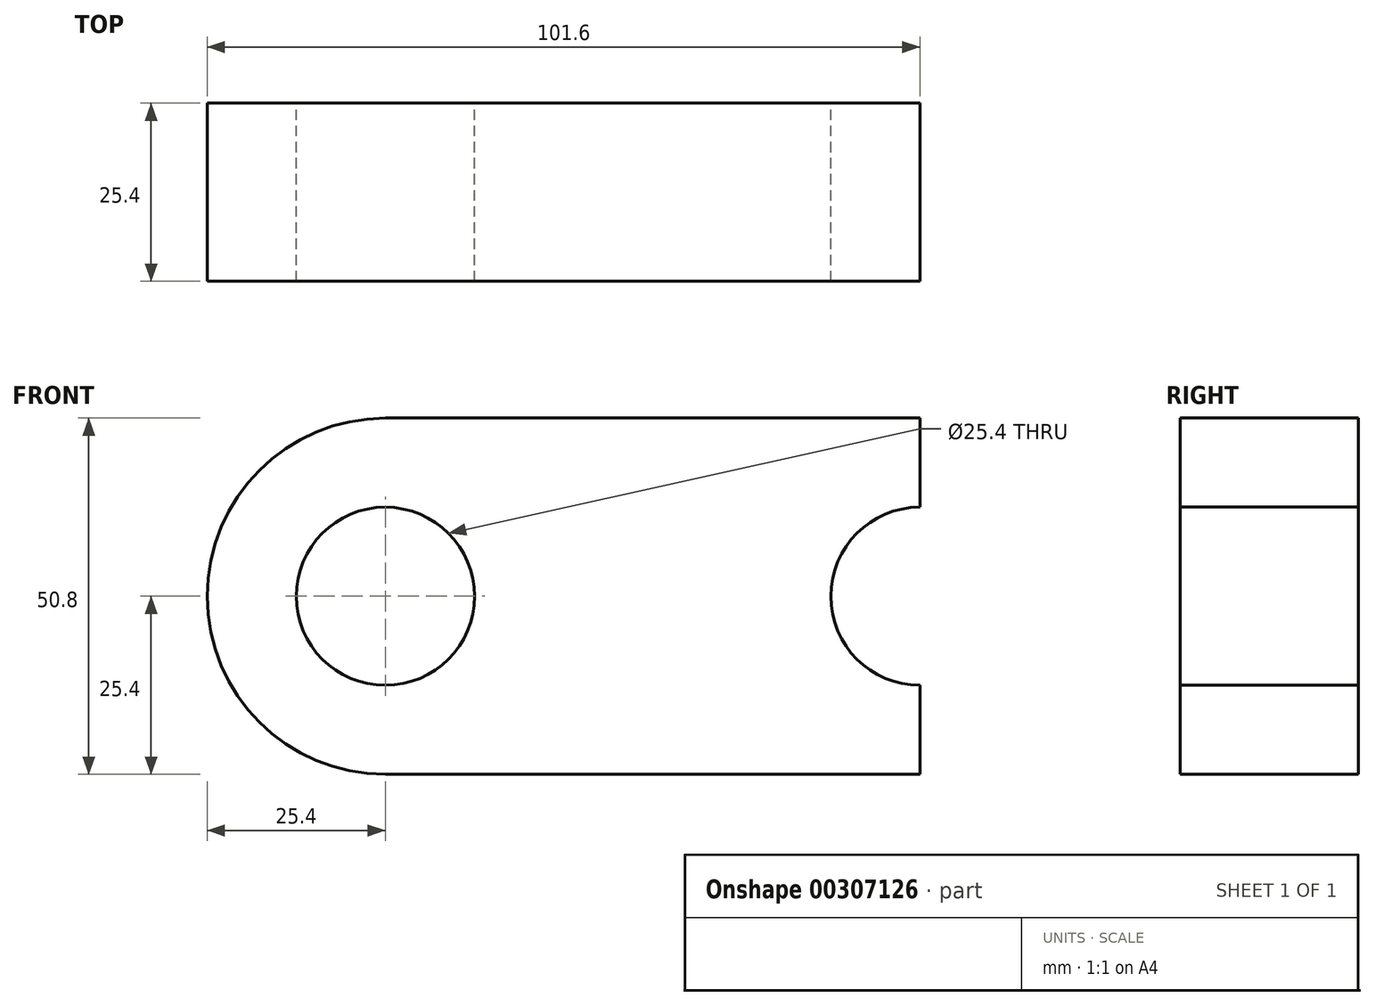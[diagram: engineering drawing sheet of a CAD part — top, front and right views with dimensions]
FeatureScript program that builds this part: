
annotation { "Feature Type Name" : "Feature", "Feature Type Description" : "" }
export const myFeature = defineFeature(function(context is Context, id is Id, definition is map)
    precondition{}
    {
        {
            var Q0;
            Q0=qCreatedBy(makeId("Front.planeOp"),FACE);
            var sketch = newSketch(context, id + "F0", { "sketchPlane" : qUnion([Q0])});
            skLineSegment(sketch, "E0.bottom", {"start": v(-38.1, 25.4) * mm, "end": v(38.1, 25.4) * mm});
            skLineSegment(sketch, "E0.top", {"start": v(-38.1, -25.4) * mm, "end": v(38.1, -25.4) * mm});
            skLineSegment(sketch, "E0.left", {"start": v(-38.1, 25.4) * mm, "end": v(-38.1, -25.4) * mm});
            skLineSegment(sketch, "E0.right", {"start": v(38.1, 25.4) * mm, "end": v(38.1, -25.4) * mm});
            skPoint(sketch, "E0.middle", {"position": v(0, 0) * mm});
            skArc(sketch, "E1", {"start": v(-38.1, 25.4) * mm, "mid": v(-63.5, 0) * mm, "end": v(-38.1, -25.4) * mm});
            skArc(sketch, "E2.MirrorCS", {"start": v(38.1, 25.4) * mm, "mid": v(63.5, 0) * mm, "end": v(38.1, -25.4) * mm});
            skCircle(sketch, "E3", {"center": v(-38.1, 0) * mm, "radius": 12.7 * mm});
            skCircle(sketch, "E4", {"center": v(38.1, 0) * mm, "radius": 12.7 * mm});
            skSolve(sketch);
        }
        {
            var Q0;
            {var subQ0=sQuery(id+"F0.wireOp",EDGE,"E1");Q0=makeQuery(id+"F0.imprint","IMPRINT",FACE,{"disambiguationData":[TD([[makeQuery(id+"F0.imprint","IMPRINT",EDGE,{"derivedFrom":subQ0}),1.0]])]});}
            var Q1;
            {var subQ5=sQuery(id+"F0.wireOp",EDGE,"E0.bottom");Q1=makeQuery(id+"F0.imprint","IMPRINT",FACE,{"disambiguationData":[TD([[makeQuery(id+"F0.imprint","IMPRINT",EDGE,{"derivedFrom":subQ5}),-1.0]])]});}
            var Q2;
            {var subQ0=sQuery(id+"F0.wireOp",EDGE,"E2.MirrorCS");Q2=makeQuery(id+"F0.imprint","IMPRINT",FACE,{"disambiguationData":[TD([[makeQuery(id+"F0.imprint","IMPRINT",EDGE,{"derivedFrom":subQ0}),-1.0]])]});}
            extrude(context, id + "F1", {"entities" : qUnion([Q0, Q1, Q2]), "depth" : 25.4 * mm});
        }
    });
